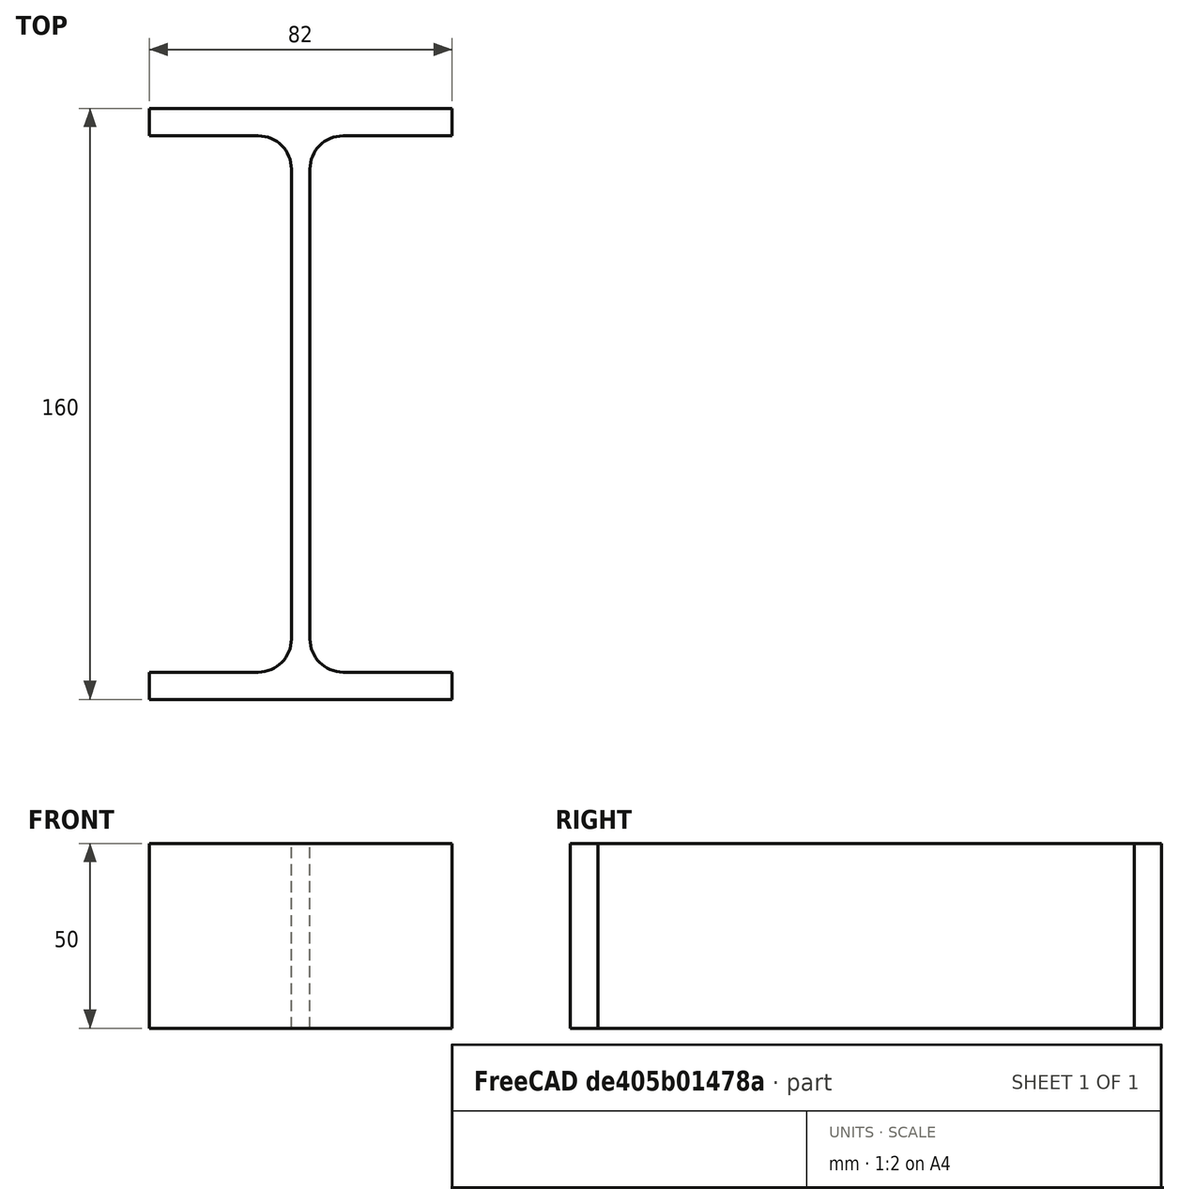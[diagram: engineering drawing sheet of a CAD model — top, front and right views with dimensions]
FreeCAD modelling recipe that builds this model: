
FCSTD DOCUMENT  (FreeCAD 0.15R4671 (Git))
Label: IPE-Profile 160 DIN1025-5 S235JR
License: All rights reserved
LicenseURL: http://en.wikipedia.org/wiki/All_rights_reserved
objects: Sketcher::SketchObject×1, Part::Extrusion×1
note: 2 computed .brp shape members not serialized (recipe doc carries the construction recipe); baked Part::Feature solids carry a one-line shape summary decoded from their .brp

FEATURE [Sketcher::SketchObject] Sketch
  sketch-geometry (16):
    g0: LineSegment StartX=2.5 StartY=-63.6 StartZ=0 EndX=2.5 EndY=63.6 EndZ=0
    g1: LineSegment StartX=11.5 StartY=72.6 StartZ=0 EndX=41 EndY=72.6 EndZ=0
    g2: LineSegment StartX=41 StartY=72.6 StartZ=0 EndX=41 EndY=80 EndZ=0
    g3: LineSegment StartX=41 StartY=80 StartZ=0 EndX=-41 EndY=80 EndZ=0
    g4: LineSegment StartX=-41 StartY=80 StartZ=0 EndX=-41 EndY=72.6 EndZ=0
    g5: LineSegment StartX=-41 StartY=72.6 StartZ=0 EndX=-11.5 EndY=72.6 EndZ=0
    g6: LineSegment StartX=-2.5 StartY=63.6 StartZ=0 EndX=-2.5 EndY=-63.6 EndZ=0
    g7: LineSegment StartX=-11.5 StartY=-72.6 StartZ=0 EndX=-41 EndY=-72.6 EndZ=0
    g8: LineSegment StartX=-41 StartY=-72.6 StartZ=0 EndX=-41 EndY=-80 EndZ=0
    g9: LineSegment StartX=-41 StartY=-80 StartZ=0 EndX=41 EndY=-80 EndZ=0
    g10: LineSegment StartX=41 StartY=-80 StartZ=0 EndX=41 EndY=-72.6 EndZ=0
    g11: LineSegment StartX=41 StartY=-72.6 StartZ=0 EndX=11.5 EndY=-72.6 EndZ=0
    g12: ArcOfCircle CenterX=11.5 CenterY=63.6 CenterZ=0 NormalX=0 NormalY=0 NormalZ=1 Radius=9 StartAngle=1.5708 EndAngle=3.14159
    g13: ArcOfCircle CenterX=11.5 CenterY=-63.6 CenterZ=0 NormalX=0 NormalY=0 NormalZ=1 Radius=9 StartAngle=3.14159 EndAngle=4.71239
    g14: ArcOfCircle CenterX=-11.5 CenterY=63.6 CenterZ=0 NormalX=0 NormalY=0 NormalZ=1 Radius=9 StartAngle=0 EndAngle=1.5708
    g15: ArcOfCircle CenterX=-11.5 CenterY=-63.6 CenterZ=0 NormalX=0 NormalY=0 NormalZ=1 Radius=9 StartAngle=4.71239 EndAngle=6.28319
  constraints (42):
    c: Vertical(g0)
    c: Coincident(g2,g1)
    c: Vertical(g2)
    c: Coincident(g3,g2)
    c: Coincident(g4,g3)
    c: Vertical(g4)
    c: Coincident(g5,g4)
    c: Horizontal(g5)
    c: Vertical(g6)
    c: Horizontal(g7)
    c: Coincident(g8,g7)
    c: Vertical(g8)
    c: Coincident(g9,g8)
    c: Horizontal(g9)
    c: Coincident(g10,g9)
    c: Vertical(g10)
    c: Coincident(g11,g10)
    c: Horizontal(g11)
    c: Tangent(g1,g12) = 1.5708
    c: Tangent(g0,g12) = 1.5708
    c: Tangent(g0,g13) = 1.5708
    c: Tangent(g11,g13) = 1.5708
    c: Tangent(g5,g14) = 1.5708
    c: Tangent(g6,g14) = 1.5708
    c: Tangent(g6,g15) = 1.5708
    c: Tangent(g7,g15) = 1.5708
    c: Equal(g3,g9)
    c: Equal(g2,g4)
    c: Equal(g4,g8)
    c: Equal(g8,g10)
    c: Equal(g12,g14)
    c: Equal(g14,g15)
    c: Equal(g15,g13)
    c: Symmetric(g2,g3,g-2)
    c: Symmetric(g9,g8,g-2)
    c: Symmetric(g0,g6,g-2)
    c: Symmetric(g2,g9,g-1)
    c: DistanceY(g2,g9) = -160
    c: DistanceX(g3) = -82
    c: DistanceX(g0,g6) = -5
    c: DistanceY(g2) = 7.4
    c: Radius(g12) = 9
FEATURE [Part::Extrusion] Extrude  label="IPE-Profile 160 DIN1025-5 S235JR"
  Base = -> Sketch
  Dir = (0,0,50)
  Solid = true
